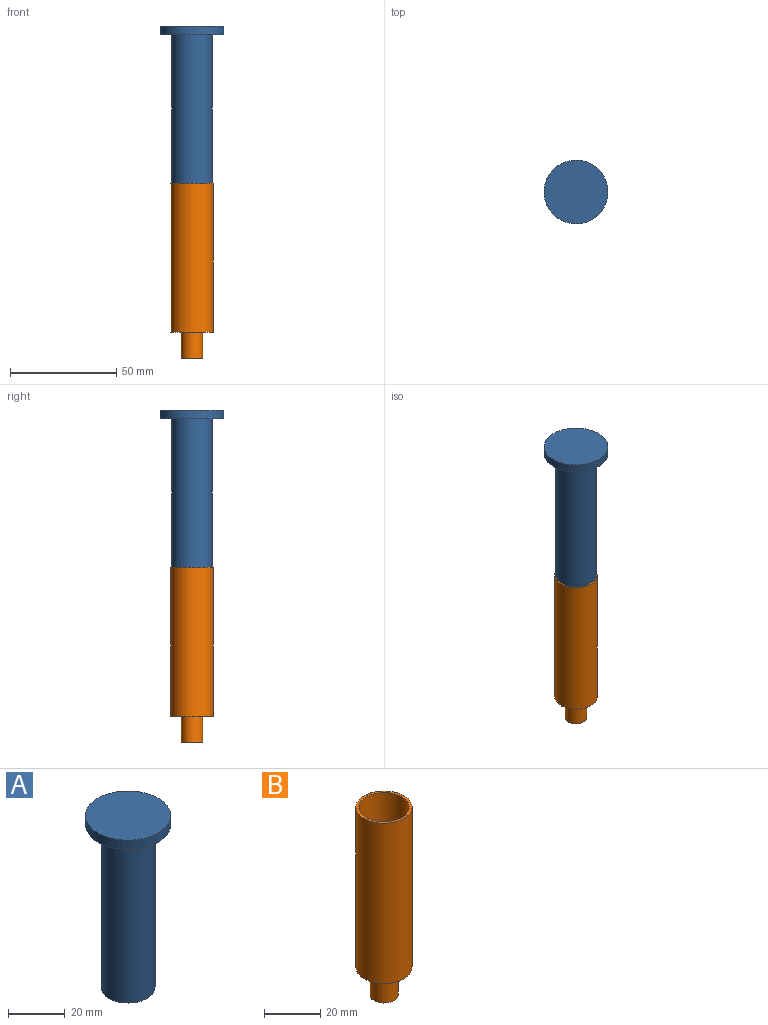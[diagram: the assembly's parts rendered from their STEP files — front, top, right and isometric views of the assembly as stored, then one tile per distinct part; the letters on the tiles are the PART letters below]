
ASSEMBLY  parts=2 mates=1
PART A: 5 faces, bbox 30x30x74 mm
  f0: cylinder r=9.5mm len=70mm, axis (0,0,-1), area 4178.3mm2, adj f1,f4
  f1: plane 19x19mm, normal (0,0,-1), area 283.5mm2, adj f0
  f2: cylinder r=15mm len=30mm, axis (0,0,-1), area 377mm2, adj f3,f4
  f3: plane 30x30mm, normal (0,0,1), area 706.9mm2, adj f2
  f4: plane 30x30mm, normal (0,0,-1), area 423.3mm2, adj f0,f2
PART B: 8 faces, bbox 20x20x82 mm
  f0: cylinder r=10mm len=70mm, axis (0,0,-1), area 4398.2mm2, adj f1,f2
  f1: plane 20x20mm, normal (0,0,1), area 59.7mm2, adj f0,f3
  f2: plane 20x20mm, normal (0,0,-1), area 235.6mm2, adj f0,f5
  f3: cylinder r=9mm len=69mm, axis (0,0,-1), area 3901.9mm2, adj f1,f4
  f4: plane 18x18mm, normal (0,0,1), area 190.9mm2, adj f3,f7
  f5: cylinder r=5mm len=12mm, axis (0,0,1), area 377mm2, adj f2,f6
  f6: plane 10x10mm, normal (0,0,-1), area 14.9mm2, adj f5,f7
  f7: cylinder r=4.5mm len=13mm, axis (0,0,-1), area 367.6mm2, adj f4,f6
PLACE A t=(46.19,18.84,74.21)mm
PLACE B t=(46.19,18.84,4.21)mm
MATE slider A.f0 <-> B.f0  axis (0,0,-1) through (46.19,18.84,74.21)mm
